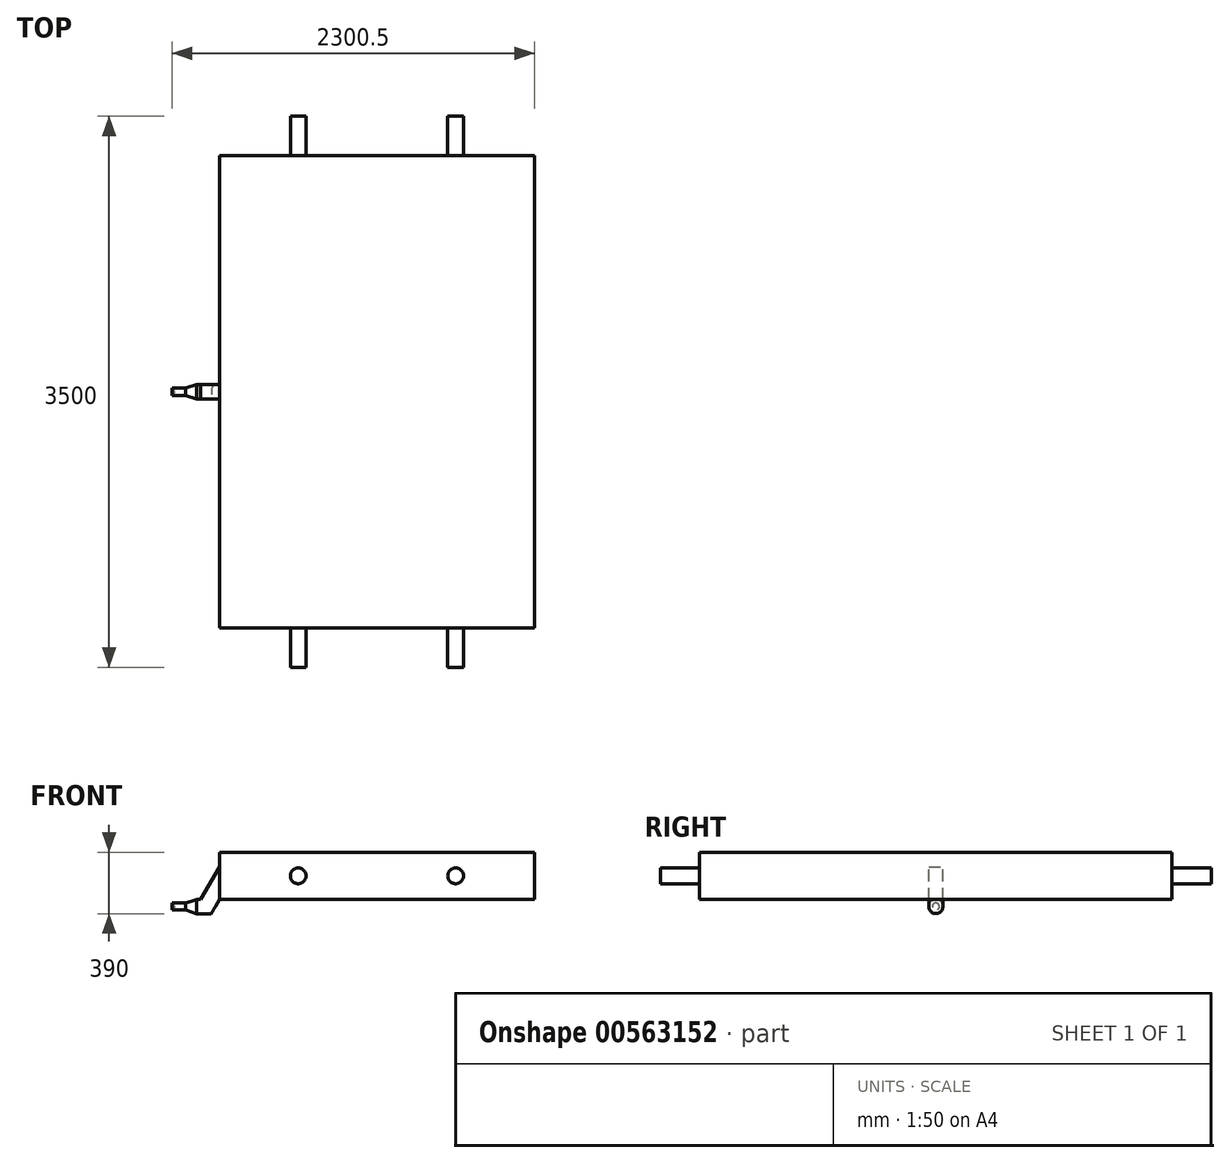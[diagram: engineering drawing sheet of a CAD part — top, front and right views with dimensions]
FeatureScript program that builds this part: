
annotation { "Feature Type Name" : "Feature", "Feature Type Description" : "" }
export const myFeature = defineFeature(function(context is Context, id is Id, definition is map)
    precondition{}
    {
        {
            var Q0;
            Q0=qCreatedBy(makeId("Front.planeOp"),FACE);
            var sketch = newSketch(context, id + "F0", { "sketchPlane" : qUnion([Q0])});
            skLineSegment(sketch, "E0.left", {"start": v(0, 0) * mm, "end": v(-16.12, 22.5) * mm});
            skLineSegment(sketch, "E0.right", {"start": v(-86.12, 0) * mm, "end": v(-102.24, 22.5) * mm});
            skLineSegment(sketch, "E1", {"start": v(-16.12, 22.5) * mm, "end": v(53.88, 22.5) * mm});
            skLineSegment(sketch, "E2", {"start": v(53.88, 22.5) * mm, "end": v(53.88, 0) * mm});
            skLineSegment(sketch, "E3", {"start": v(53.88, 0) * mm, "end": v(0, 0) * mm});
            skLineSegment(sketch, "E4", {"start": v(-86.12, 0) * mm, "end": v(0, 0) * mm});
            skLineSegment(sketch, "E5", {"start": v(-16.12, 22.5) * mm, "end": v(-102.24, 22.5) * mm});
            skLineSegment(sketch, "E6", {"start": v(53.88, 22.5) * mm, "end": v(53.88, 45) * mm});
            skLineSegment(sketch, "E7", {"start": v(53.88, 45) * mm, "end": v(-16.12, 22.5) * mm});
            skLineSegment(sketch, "E8", {"start": v(53.88, 45) * mm, "end": v(53.88, -45) * mm});
            skPoint(sketch, "E8.endSnap0", {"position": v(53.88, 11.25) * mm});
            skLineSegment(sketch, "E9", {"start": v(53.88, -45) * mm, "end": v(146.3, -45) * mm});
            skLineSegment(sketch, "E10", {"start": v(146.3, -45) * mm, "end": v(198.26, 45) * mm});
            skLineSegment(sketch, "E11", {"start": v(53.88, 45) * mm, "end": v(78.88, 45) * mm});
            skLineSegment(sketch, "E12", {"start": v(198.26, 45) * mm, "end": v(2198.26, 45) * mm});
            skLineSegment(sketch, "E13", {"start": v(2198.26, 345) * mm, "end": v(198.26, 345) * mm});
            skLineSegment(sketch, "E14", {"start": v(2198.26, 345) * mm, "end": v(2198.26, 135) * mm});
            skLineSegment(sketch, "E15", {"start": v(2198.26, 135) * mm, "end": v(2198.26, 45) * mm});
            skLineSegment(sketch, "E16", {"start": v(198.26, 45) * mm, "end": v(198.26, 345) * mm});
            skLineSegment(sketch, "E17", {"start": v(78.88, 45) * mm, "end": v(198.26, 251.77) * mm});
            skLineSegment(sketch, "E18", {"start": v(1198.26, 195) * mm, "end": v(1698.26, 195) * mm, "construction": true});
            skLineSegment(sketch, "E19", {"start": v(1198.26, 195) * mm, "end": v(698.26, 195) * mm, "construction": true});
            skCircle(sketch, "E20", {"center": v(1698.26, 195) * mm, "radius": 50 * mm});
            skCircle(sketch, "E21", {"center": v(698.26, 195) * mm, "radius": 50 * mm});
            skSolve(sketch);
        }
        {
            var Q0;
            {var subQ0=sQuery(id+"F0.wireOp",EDGE,"E1");Q0=makeQuery(id+"F0.imprint","IMPRINT",FACE,{"disambiguationData":[TD([[makeQuery(id+"F0.imprint","IMPRINT",EDGE,{"derivedFrom":subQ0}),1.0]])]});}
            var Q1;
            Q1=makeQuery(id+"F0.imprint","IMPRINT",FACE,{"disambiguationData":[TD([[makeQuery(id+"F0.imprint","IMPRINT",EDGE,{"derivedFrom":sQuery(id+"F0.wireOp",EDGE,"E0.left")}),-1.0]])]});
            var Q2;
            Q2=makeQuery(id+"F0.imprint","IMPRINT",FACE,{"disambiguationData":[TD([[makeQuery(id+"F0.imprint","IMPRINT",EDGE,{"derivedFrom":sQuery(id+"F0.wireOp",EDGE,"E0.left")}),1.0]])]});
            var Q3;
            Q3=sQuery(id+"F0.wireOp",EDGE,"E4");
            revolve(context, id + "F1", {"entities" : qUnion([Q0, Q1, Q2]), "axis" : qUnion([Q3]), "revolveType" : RevolveType.FULL});
        }
        {
            var Q0;
            {var subQ0=sQuery(id+"F0.wireOp",EDGE,"E9");Q0=makeQuery(id+"F0.imprint","IMPRINT",FACE,{"disambiguationData":[TD([[makeQuery(id+"F0.imprint","IMPRINT",EDGE,{"derivedFrom":subQ0}),1.0]])]});}
            extrude(context, id + "F2", {"entities" : qUnion([Q0]), "operationType" : NewBodyOperationType.ADD, "endBound" : BoundingType.SYMMETRIC, "depth" : 90 * mm, "offsetDistance" : 25 * mm});
        }
        {
            var Q0;
            Q0=makeQuery(id+"F2.opExtrude","CAP_EDGE",EDGE,{"disambiguationData":[OSD([sQuery(id+"F0.wireOp",EDGE,"p91IUJKM-OsKN-bIau-hd4h-NLhWMxrZFuZe")])],"isStart":true});
            var Q1;
            Q1=makeQuery(id+"F2.opExtrude","CAP_EDGE",EDGE,{"disambiguationData":[OSD([sQuery(id+"F0.wireOp",EDGE,"p91IUJKM-OsKN-bIau-hd4h-NLhWMxrZFuZe")])],"isStart":false});
            var Q2;
            Q2=makeQuery(id+"F2.opExtrude","CAP_EDGE",EDGE,{"disambiguationData":[OSD([sQuery(id+"F0.wireOp",EDGE,"E9")])],"isStart":true});
            var Q3;
            Q3=makeQuery(id+"F2.opExtrude","CAP_EDGE",EDGE,{"disambiguationData":[OSD([sQuery(id+"F0.wireOp",EDGE,"E9")])],"isStart":false});
            fillet(context, id + "F3", {"entities" : qUnion([Q0, Q1, Q2, Q3]), "radius" : 45 * mm, "tangentPropagation" : true, "allowEdgeOverflow" : false});
        }
        {
            var Q0;
            {var subQ1=sQuery(id+"F0.wireOp",EDGE,"E12");Q0=makeQuery(id+"F0.imprint","IMPRINT",FACE,{"disambiguationData":[TD([[makeQuery(id+"F0.imprint","IMPRINT",EDGE,{"derivedFrom":subQ1}),1.0]])]});}
            extrude(context, id + "F4", {"entities" : qUnion([Q0]), "endBound" : BoundingType.SYMMETRIC, "depth" : 3000 * mm, "offsetDistance" : 25 * mm, "hasSecondDirection" : true, "secondDirectionOppositeDirection" : true, "secondDirectionDepth" : 200 * mm});
        }
        {
            var Q0;
            Q0=makeQuery(id+"F0.imprint","IMPRINT",FACE,{"disambiguationData":[TD([[makeQuery(id+"F0.imprint","IMPRINT",EDGE,{"derivedFrom":sQuery(id+"F0.wireOp",EDGE,"E20")}),1.0]])]});
            var Q1;
            Q1=makeQuery(id+"F0.imprint","IMPRINT",FACE,{"disambiguationData":[TD([[makeQuery(id+"F0.imprint","IMPRINT",EDGE,{"derivedFrom":sQuery(id+"F0.wireOp",EDGE,"E21")}),1.0]])]});
            extrude(context, id + "F5", {"entities" : qUnion([Q0, Q1]), "operationType" : NewBodyOperationType.ADD, "endBound" : BoundingType.SYMMETRIC, "oppositeDirection" : true, "depth" : 3500 * mm, "offsetDistance" : 25 * mm, "hasSecondDirection" : true, "secondDirectionOppositeDirection" : true, "secondDirectionDepth" : 1500 * mm});
        }
    });
